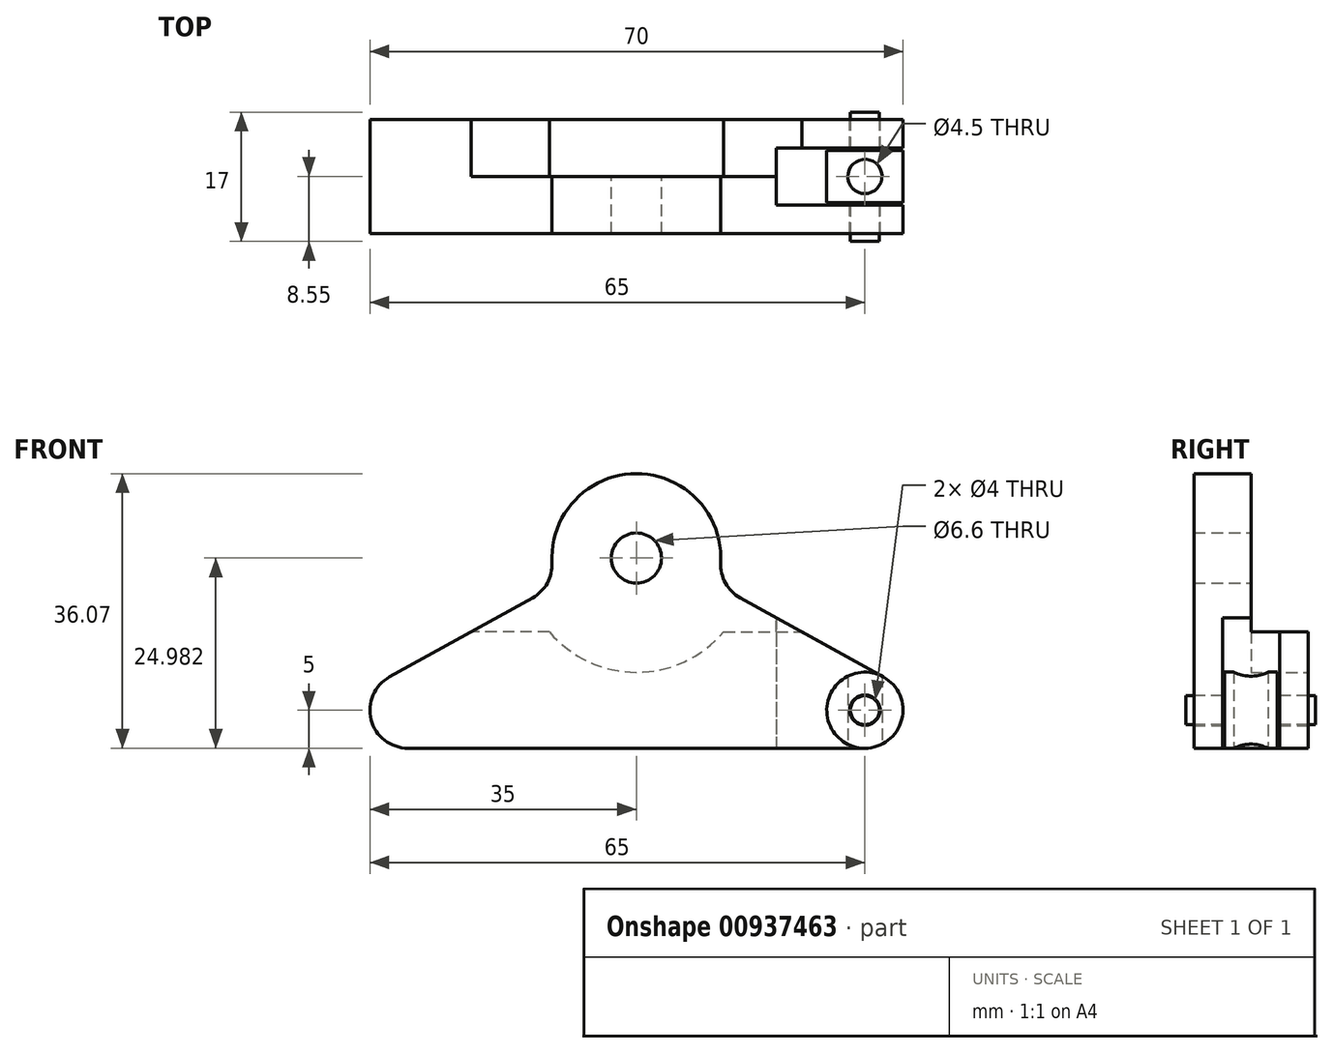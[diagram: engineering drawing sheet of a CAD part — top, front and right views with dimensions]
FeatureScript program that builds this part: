
annotation { "Feature Type Name" : "Feature", "Feature Type Description" : "" }
export const myFeature = defineFeature(function(context is Context, id is Id, definition is map)
    precondition{}
    {
        {
            var Q0;
            Q0=qCreatedBy(makeId("Front.planeOp"),FACE);
            var sketch = newSketch(context, id + "F0", { "sketchPlane" : qUnion([Q0])});
            skLineSegment(sketch, "E0", {"start": v(-32.42, 9.38) * mm, "end": v(-10.52, 21.48) * mm});
            skLineSegment(sketch, "E1", {"start": v(10.52, 21.48) * mm, "end": v(32.42, 9.38) * mm});
            skLineSegment(sketch, "E2", {"start": v(30, 0) * mm, "end": v(-30, 0) * mm});
            skArc(sketch, "E3", {"start": v(10.52, 21.48) * mm, "mid": v(0, 36.07) * mm, "end": v(-10.52, 21.48) * mm});
            skPoint(sketch, "E4.visualSharp", {"position": v(-49.38, 0) * mm});
            skArc(sketch, "E4.filletArc", {"start": v(-32.42, 9.38) * mm, "mid": v(-34.84, 3.75) * mm, "end": v(-30, 0) * mm});
            skPoint(sketch, "E5.visualSharp", {"position": v(49.38, 0) * mm});
            skArc(sketch, "E5.filletArc", {"start": v(30, 0) * mm, "mid": v(34.84, 3.75) * mm, "end": v(32.42, 9.38) * mm});
            skPoint(sketch, "E6.orphan", {"position": v(0, 27.3) * mm});
            skSolve(sketch);
        }
        {
            var Q0;
            Q0 = qSketchRegion(id + "F0", true);
            extrude(context, id + "F1", {"entities" : qUnion([Q0]), "endBound" : BoundingType.SYMMETRIC, "depth" : 15 * mm, "offsetDistance" : 25 * mm});
        }
        {
            var Q0;
            Q0=makeQuery(id+"F1.opExtrude","CAP_FACE",FACE,{"disambiguationData":[OSD([sQuery(id+"F0.wireOp",EDGE,"E0"),sQuery(id+"F0.wireOp",EDGE,"E1"),sQuery(id+"F0.wireOp",EDGE,"E2"),sQuery(id+"F0.wireOp",EDGE,"E3"),sQuery(id+"F0.wireOp",EDGE,"E4.filletArc"),sQuery(id+"F0.wireOp",EDGE,"E5.filletArc")])],"isStart":true});
            var sketch = newSketch(context, id + "F2", { "sketchPlane" : qUnion([Q0])});
            skArc(sketch, "E7", {"start": v(11.04, 35.14) * mm, "mid": v(0, 39.98) * mm, "end": v(-11.04, 35.14) * mm});
            skLineSegment(sketch, "E8", {"start": v(11.44, 15.28) * mm, "end": v(29.3, 15.28) * mm});
            skLineSegment(sketch, "E9", {"start": v(29.3, 15.28) * mm, "end": v(11.04, 35.14) * mm});
            skLineSegment(sketch, "E10.MirrorCS", {"start": v(-29.3, 15.28) * mm, "end": v(-11.04, 35.14) * mm});
            skLineSegment(sketch, "E11.MirrorCS", {"start": v(-11.44, 15.28) * mm, "end": v(-29.3, 15.28) * mm});
            skArc(sketch, "E12.trimOffspring", {"start": v(-11.44, 15.28) * mm, "mid": v(0, 9.98) * mm, "end": v(11.44, 15.28) * mm});
            skSolve(sketch);
        }
        {
            var Q0;
            Q0 = qSketchRegion(id + "F2", true);
            extrude(context, id + "F3", {"entities" : qUnion([Q0]), "operationType" : NewBodyOperationType.REMOVE, "oppositeDirection" : true, "depth" : 7.5 * mm, "offsetDistance" : 25 * mm});
        }
        {
            var Q0;
            Q0=sQuery(id+"F0.wireOp",VERTEX,"E3.center");
            var Q1;
            Q1=makeQuery(id+"F1.opExtrude","SWEPT_BODY",BODY,{"disambiguationData":[OSD([sQuery(id+"F0.wireOp",EDGE,"E0"),sQuery(id+"F0.wireOp",EDGE,"E1"),sQuery(id+"F0.wireOp",EDGE,"E2"),sQuery(id+"F0.wireOp",EDGE,"E3"),sQuery(id+"F0.wireOp",EDGE,"E4.filletArc"),sQuery(id+"F0.wireOp",EDGE,"E5.filletArc")])]});
            hole(context, id + "F4", {"style" : HoleStyle.SIMPLE, "endStyle" : HoleEndStyle.THROUGH, "oppositeDirection" : true, "standardTappedOrClearance" : lookupTablePath({ "fit" : "Normal", "standard" : "ISO", "size" : "M6", "type" : "Clearance" }), "standardBlindInLast" : lookupTablePath({ "fit" : "Normal", "standard" : "ISO", "engagement" : "75%", "pitch" : "1 mm", "size" : "M6", "type" : "Clearance & tapped" }), "holeDiameter" : 6.6 * mm, "majorDiameter" : 5 * mm, "isTappedThrough" : true, "tappedDepth" : 12 * mm, "tapClearance" : 3, "locations" : qUnion([Q0]), "scope" : qUnion([Q1])});
        }
        {
            var Q0;
            Q0=makeQuery(id+"F1.opExtrude","CAP_FACE",FACE,{"disambiguationData":[OSD([sQuery(id+"F0.wireOp",EDGE,"E0"),sQuery(id+"F0.wireOp",EDGE,"E1"),sQuery(id+"F0.wireOp",EDGE,"E2"),sQuery(id+"F0.wireOp",EDGE,"E3"),sQuery(id+"F0.wireOp",EDGE,"E4.filletArc"),sQuery(id+"F0.wireOp",EDGE,"E5.filletArc")])],"isStart":true});
            var sketch = newSketch(context, id + "F5", { "sketchPlane" : qUnion([Q0])});
            skArc(sketch, "E13.0", {"start": v(-30, 0) * mm, "mid": v(-34.84, 3.75) * mm, "end": v(-32.42, 9.38) * mm});
            skLineSegment(sketch, "E14", {"start": v(-36.16, 0) * mm, "end": v(-30, 0) * mm});
            skLineSegment(sketch, "E15", {"start": v(-36.16, 0) * mm, "end": v(-36.16, 7.3) * mm});
            skLineSegment(sketch, "E16", {"start": v(-32.42, 9.38) * mm, "end": v(-36.16, 7.3) * mm});
            skSolve(sketch);
        }
        {
            var Q0;
            Q0=makeQuery(id+"F1.opExtrude","SWEPT_EDGE",EDGE,{"disambiguationData":[OSD([sQuery(id+"F0.wireOp",EDGE,"E1"),sQuery(id+"F0.wireOp",EDGE,"E3")])]});
            var Q1;
            Q1=makeQuery(id+"F1.opExtrude","SWEPT_EDGE",EDGE,{"disambiguationData":[OSD([sQuery(id+"F0.wireOp",EDGE,"E0"),sQuery(id+"F0.wireOp",EDGE,"E3")])]});
            fillet(context, id + "F6", {"entities" : qUnion([Q0, Q1]), "radius" : 5 * mm, "tangentPropagation" : true, "allowEdgeOverflow" : false});
        }
        {
            var Q0;
            Q0=sQuery(id+"F5.wireOp",VERTEX,"E13.0.center");
            var Q1;
            Q1=makeQuery(id+"F1.opExtrude","SWEPT_BODY",BODY,{"disambiguationData":[OSD([sQuery(id+"F0.wireOp",EDGE,"E0"),sQuery(id+"F0.wireOp",EDGE,"E1"),sQuery(id+"F0.wireOp",EDGE,"E2"),sQuery(id+"F0.wireOp",EDGE,"E3"),sQuery(id+"F0.wireOp",EDGE,"E4.filletArc"),sQuery(id+"F0.wireOp",EDGE,"E5.filletArc")])]});
            hole(context, id + "F7", {"style" : HoleStyle.SIMPLE, "endStyle" : HoleEndStyle.THROUGH, "holeDiameter" : 4 * mm, "majorDiameter" : 5 * mm, "isTappedThrough" : true, "tappedDepth" : 12 * mm, "tapClearance" : 3, "locations" : qUnion([Q0]), "scope" : qUnion([Q1])});
        }
        {
            var Q0;
            Q0=makeQuery(id+"FyVZ86yOLYinZwO_1.boolean.opBoolean","COPY",FACE,{"derivedFrom":makeQuery(id+"FyVZ86yOLYinZwO_1.opExtrude","CAP_FACE",FACE,{"disambiguationData":[OSD([sQuery(id+"F5.wireOp",EDGE,"E13.0"),sQuery(id+"F5.wireOp",EDGE,"E14"),sQuery(id+"F5.wireOp",EDGE,"E15"),sQuery(id+"F5.wireOp",EDGE,"E16")])],"isStart":false})});
            var sketch = newSketch(context, id + "F8", { "sketchPlane" : qUnion([Q0])});
            skArc(sketch, "E17", {"start": v(-43.68, 10.93) * mm, "mid": v(-45.19, 12) * mm, "end": v(-46.9, 12.7) * mm});
            skLineSegment(sketch, "E18", {"start": v(-46.9, 12.7) * mm, "end": v(-41.36, 16.67) * mm});
            skLineSegment(sketch, "E19", {"start": v(-41.36, 16.67) * mm, "end": v(-43.68, 10.93) * mm});
            skSolve(sketch);
        }
        {
            var Q0;
            Q0=qCreatedBy(makeId("Front.planeOp"),FACE);
            var sketch = newSketch(context, id + "F9", { "sketchPlane" : qUnion([Q0])});
            skArc(sketch, "E20.0", {"start": v(30, 0) * mm, "mid": v(34.84, 3.75) * mm, "end": v(32.42, 9.38) * mm});
            skLineSegment(sketch, "E21", {"start": v(30, 5) * mm, "end": v(16.76, 31) * mm, "construction": true});
            skLineSegment(sketch, "E22", {"start": v(32.42, 9.38) * mm, "end": v(18.38, 17.14) * mm});
            skLineSegment(sketch, "E23", {"start": v(18.38, 17.14) * mm, "end": v(18.38, 0) * mm});
            skLineSegment(sketch, "E24", {"start": v(18.38, 0) * mm, "end": v(30, 0) * mm});
            skSolve(sketch);
        }
        {
            var Q0;
            Q0 = qSketchRegion(id + "F9", true);
            extrude(context, id + "F10", {"entities" : qUnion([Q0]), "operationType" : NewBodyOperationType.REMOVE, "endBound" : BoundingType.SYMMETRIC, "oppositeDirection" : true, "depth" : 7.5 * mm, "offsetDistance" : 25 * mm});
        }
        {
            var Q0;
            Q0=qCreatedBy(makeId("Front.planeOp"),FACE);
            var sketch = newSketch(context, id + "F11", { "sketchPlane" : qUnion([Q0])});
            skCircle(sketch, "E25", {"center": v(30, 5) * mm, "radius": 5 * mm});
            skSolve(sketch);
        }
        {
            var Q0;
            Q0 = qSketchRegion(id + "F11", true);
            var Q1;
            Q1=sQuery(id+"F11.wireOp",EDGE,"E25");
            extrude(context, id + "F12", {"entities" : qUnion([Q0]), "surfaceEntities" : qUnion([Q1]), "endBound" : BoundingType.SYMMETRIC, "depth" : (7.5 - .6) * mm, "offsetDistance" : 25 * mm});
        }
        {
            var Q0;
            Q0=makeQuery(id+"F12.opExtrude","CAP_FACE",FACE,{"disambiguationData":[OSD([sQuery(id+"F11.wireOp",EDGE,"E25")])],"isStart":true});
            var sketch = newSketch(context, id + "F13", { "sketchPlane" : qUnion([Q0])});
            skCircle(sketch, "E26", {"center": v(-30, 5) * mm, "radius": 1.9 * mm});
            skSolve(sketch);
        }
        {
            var Q0;
            Q0 = qSketchRegion(id + "F13", true);
            extrude(context, id + "F14", {"entities" : qUnion([Q0]), "operationType" : NewBodyOperationType.ADD, "depth" : 5 * mm, "offsetDistance" : 25 * mm, "hasSecondDirection" : true, "secondDirectionOppositeDirection" : true, "secondDirectionDepth" : (7 + 5) * mm});
        }
        {
            var Q0;
            Q0=qCreatedBy(makeId("Top.planeOp"),FACE);
            var sketch = newSketch(context, id + "F15", { "sketchPlane" : qUnion([Q0])});
            skCircle(sketch, "E27", {"center": v(30, 0) * mm, "radius": 2.25 * mm});
            skSolve(sketch);
        }
        {
            var Q0;
            Q0 = qSketchRegion(id + "F15", true);
            extrude(context, id + "F16", {"entities" : qUnion([Q0]), "operationType" : NewBodyOperationType.REMOVE, "endBound" : BoundingType.THROUGH_ALL, "depth" : 25 * mm, "offsetDistance" : 25 * mm});
        }
    });
